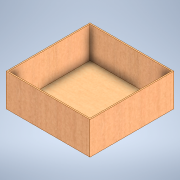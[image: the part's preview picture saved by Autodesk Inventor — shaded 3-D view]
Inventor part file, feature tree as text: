
AUTODESK INVENTOR PART (.ipt)
format: ipt  version: 2021 (Build 250183000, 183)  size: 133,632 bytes
history: native  units: mm
features: other x2, extrude x2, sketch x2
ambient origin geometry x8: Origin, YZ Plane, XZ Plane, XY Plane, X Axis, Y Axis, Z Axis, Center Point
bodies: Body1 (feature_tree)
feature tree (6):
  other  "Sólido1"
  extrude  "Extrusão1"  Depth=103.0mm
  extrude  "Extrusão2"  Depth=1.5mm
  sketch  "Esboço1"  dims[d0=103.0mm d1=103.0mm]
  sketch  "Esboço2"  dims[d2=40.0mm d3=0.0mm d4=1.5mm d5=38.5mm d6=0.0mm]
  other  "Contorno projetado1"
